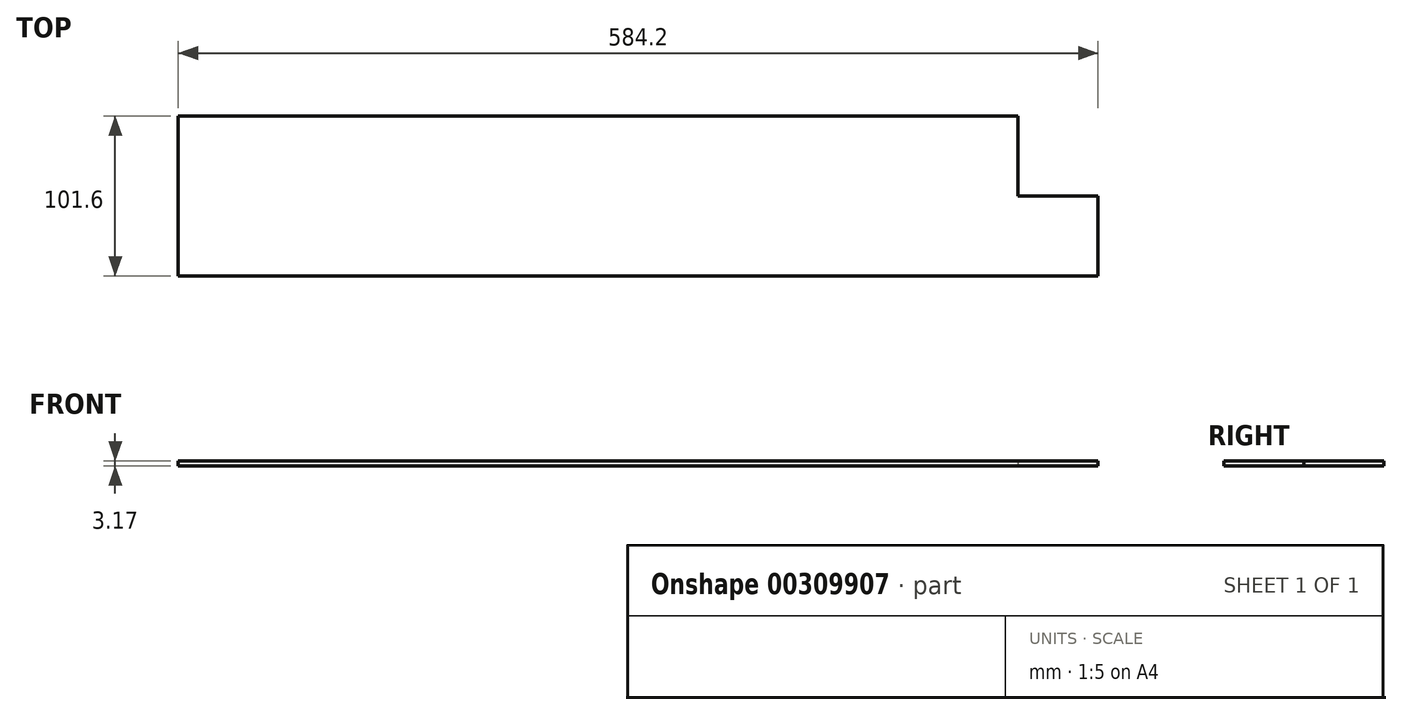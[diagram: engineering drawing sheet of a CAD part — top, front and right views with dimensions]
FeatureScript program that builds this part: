
annotation { "Feature Type Name" : "Feature", "Feature Type Description" : "" }
export const myFeature = defineFeature(function(context is Context, id is Id, definition is map)
    precondition{}
    {
        {
            var Q0;
            Q0=qCreatedBy(makeId("Top.planeOp"),FACE);
            var sketch = newSketch(context, id + "F0", { "sketchPlane" : qUnion([Q0])});
            skLineSegment(sketch, "E0.bottom", {"start": v(0, 0) * mm, "end": v(-584.2, 0) * mm});
            skLineSegment(sketch, "E0.top", {"start": v(-50.8, 101.6) * mm, "end": v(-584.2, 101.6) * mm});
            skLineSegment(sketch, "E0.left", {"start": v(0, 0) * mm, "end": v(0, 50.8) * mm});
            skLineSegment(sketch, "E0.right", {"start": v(-584.2, 0) * mm, "end": v(-584.2, 101.6) * mm});
            skLineSegment(sketch, "E1", {"start": v(-50.8, 50.8) * mm, "end": v(0, 50.8) * mm});
            skLineSegment(sketch, "E2", {"start": v(-50.8, 50.8) * mm, "end": v(-50.8, 101.6) * mm});
            skSolve(sketch);
        }
        {
            var Q0;
            Q0=makeQuery(id+"F0.imprint","IMPRINT",FACE,{"disambiguationData":[TD([[makeQuery(id+"F0.imprint","IMPRINT",EDGE,{"derivedFrom":sQuery(id+"F0.wireOp",EDGE,"E0.bottom")}),-1.0]])]});
            extrude(context, id + "F1", {"entities" : qUnion([Q0]), "depth" : 3.17 * mm});
        }
    });
